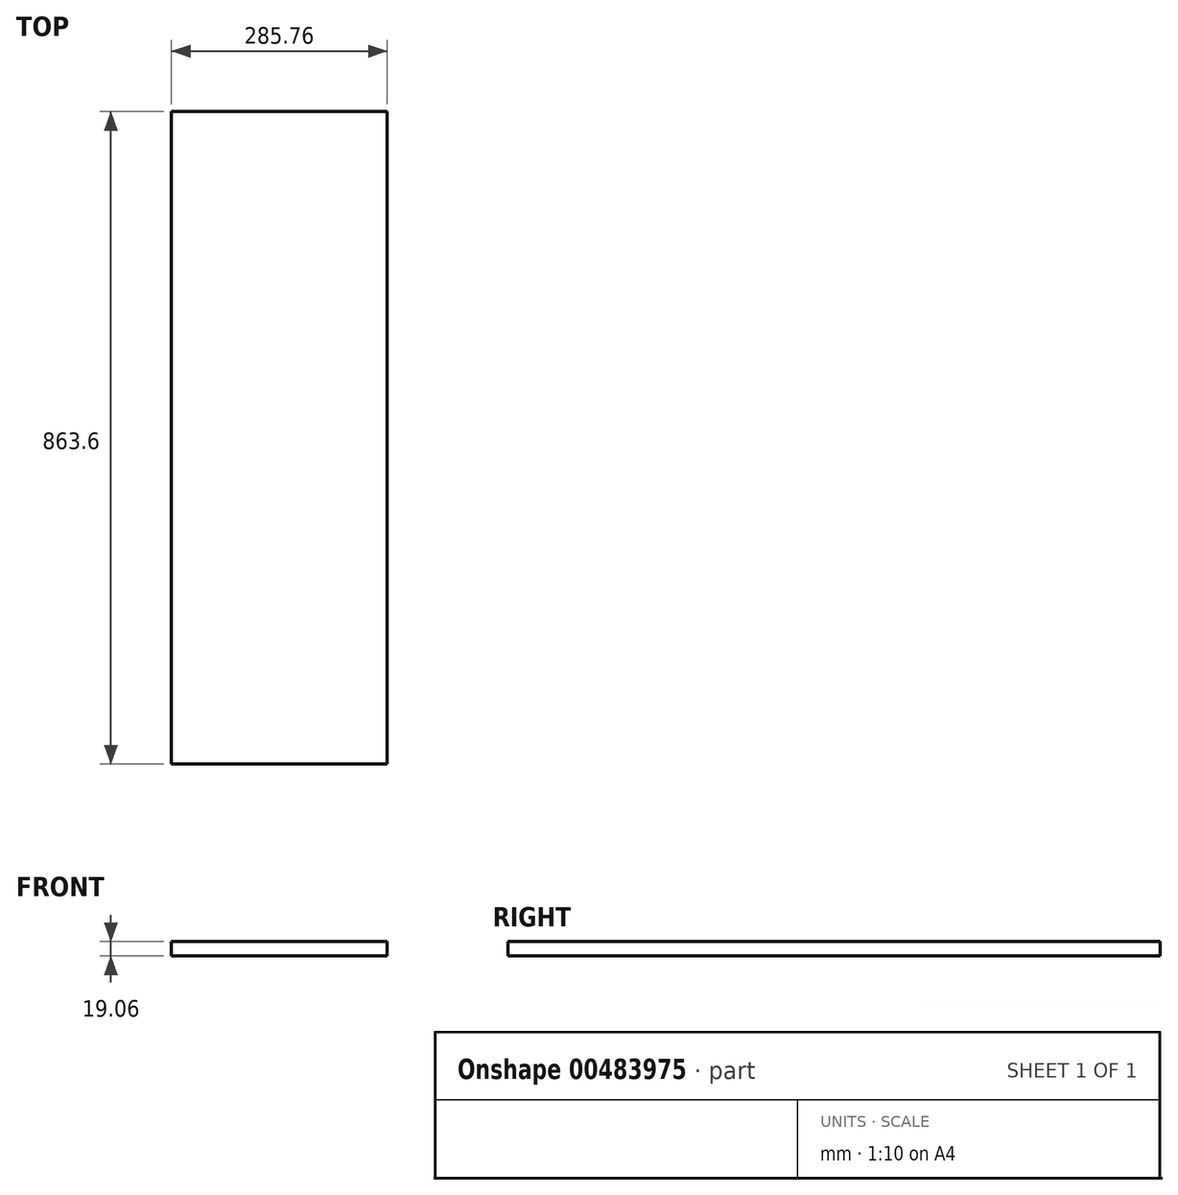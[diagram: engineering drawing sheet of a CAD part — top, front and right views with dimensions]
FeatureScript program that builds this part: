
annotation { "Feature Type Name" : "Feature", "Feature Type Description" : "" }
export const myFeature = defineFeature(function(context is Context, id is Id, definition is map)
    precondition{}
    {
        {
            var Q0;
            Q0=qCreatedBy(makeId("Front.planeOp"),FACE);
            var sketch = newSketch(context, id + "F0", { "sketchPlane" : qUnion([Q0])});
            skLineSegment(sketch, "E0.bottom", {"start": v(142.88, 9.53) * mm, "end": v(-142.88, 9.53) * mm});
            skLineSegment(sketch, "E0.top", {"start": v(142.88, -9.53) * mm, "end": v(-142.88, -9.53) * mm});
            skLineSegment(sketch, "E0.left", {"start": v(142.88, 9.53) * mm, "end": v(142.88, -9.53) * mm});
            skLineSegment(sketch, "E0.right", {"start": v(-142.88, 9.53) * mm, "end": v(-142.88, -9.53) * mm});
            skPoint(sketch, "E0.middle", {"position": v(0, 0) * mm});
            skSolve(sketch);
        }
        {
            var Q0;
            Q0 = qSketchRegion(id + "F0", true);
            extrude(context, id + "F1", {"entities" : qUnion([Q0]), "depth" : 863.6 * mm, "offsetDistance" : 25.4 * mm});
        }
    });
